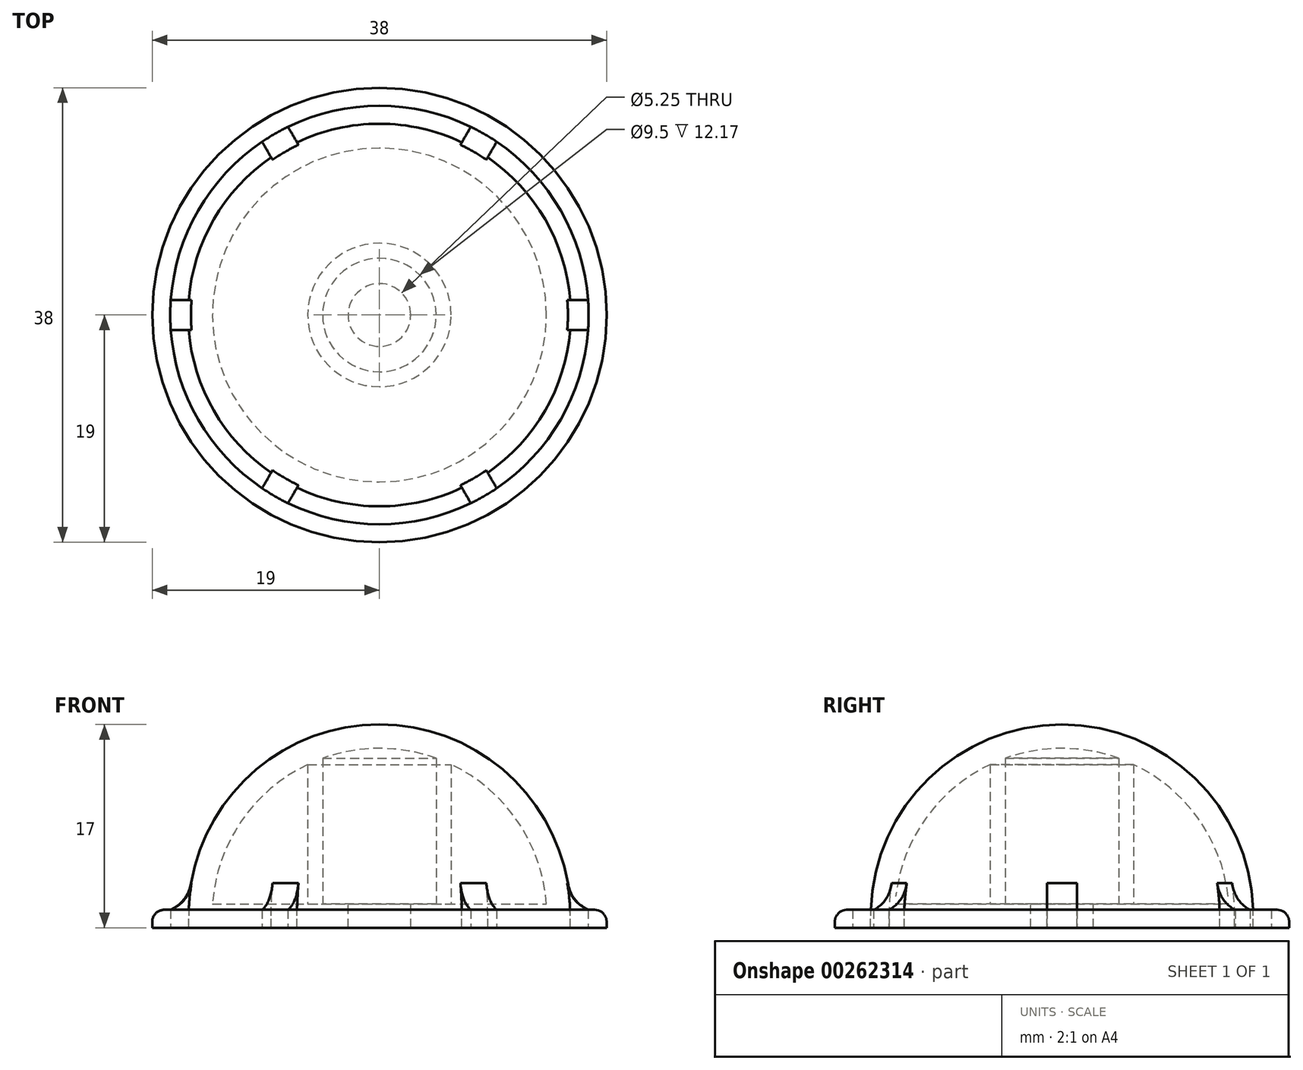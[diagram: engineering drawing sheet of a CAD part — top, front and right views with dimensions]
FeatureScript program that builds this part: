
annotation { "Feature Type Name" : "Feature", "Feature Type Description" : "" }
export const myFeature = defineFeature(function(context is Context, id is Id, definition is map)
    precondition{}
    {
        {
            var Q0;
            Q0=qCreatedBy(makeId("Top.planeOp"),FACE);
            var sketch = newSketch(context, id + "F0", { "sketchPlane" : qUnion([Q0])});
            skArc(sketch, "E0", {"start": v(0, -16) * mm, "mid": v(16, 0) * mm, "end": v(0, 16) * mm});
            skLineSegment(sketch, "E1", {"start": v(0, 16) * mm, "end": v(0, -16) * mm});
            skSolve(sketch);
        }
        {
            var Q0;
            Q0=makeQuery(id+"F0.imprint","IMPRINT",FACE,{"disambiguationData":[TD([[makeQuery(id+"F0.imprint","IMPRINT",EDGE,{"derivedFrom":sQuery(id+"F0.wireOp",EDGE,"E0")}),1.0]])]});
            var Q1;
            Q1=sQuery(id+"F0.wireOp",EDGE,"E1");
            revolve(context, id + "F1", {"entities" : qUnion([Q0]), "axis" : qUnion([Q1]), "revolveType" : RevolveType.ONE_DIRECTION, "angle" : 180 * degree});
        }
        {
            var Q0;
            Q0=makeQuery(id+"F1.opRevolve","CAP_FACE",FACE,{"disambiguationData":[OSD([sQuery(id+"F0.wireOp",EDGE,"E0"),sQuery(id+"F0.wireOp",EDGE,"E1")])],"isStart":true});
            var sketch = newSketch(context, id + "F2", { "sketchPlane" : qUnion([Q0])});
            skCircle(sketch, "E2", {"center": v(0, 0) * mm, "radius": 2.62 * mm});
            skSolve(sketch);
        }
        {
            var Q0;
            Q0=makeQuery(id+"F2.imprint","IMPRINT",FACE,{"disambiguationData":[TD([[makeQuery(id+"F2.imprint","IMPRINT",EDGE,{"derivedFrom":sQuery(id+"F2.wireOp",EDGE,"E2")}),-1.0]])]});
            extrude(context, id + "F3", {"entities" : qUnion([Q0]), "operationType" : NewBodyOperationType.ADD, "depth" : 1 * mm});
        }
        {
            var Q0;
            Q0=makeQuery(id+"F1.opRevolve","CAP_FACE",FACE,{"disambiguationData":[OSD([sQuery(id+"F0.wireOp",EDGE,"E0"),sQuery(id+"F0.wireOp",EDGE,"E1")])],"isStart":true});
            shell(context, id + "F4", {"entities" : qUnion([Q0]), "thickness" : 2 * mm});
        }
        {
            var Q0;
            Q0=makeQuery(id+"F4.opShell","OFFSET_FACE",FACE,{"disambiguationData":[OSD([sQuery(id+"F0.wireOp",EDGE,"E0"),sQuery(id+"F2.wireOp",EDGE,"E2")])]});
            var sketch = newSketch(context, id + "F5", { "sketchPlane" : qUnion([Q0])});
            skCircle(sketch, "E3", {"center": v(0, 0) * mm, "radius": 6 * mm});
            skCircle(sketch, "E4", {"center": v(0, 0) * mm, "radius": 4.75 * mm});
            skSolve(sketch);
        }
        {
            var Q0;
            Q0=makeQuery(id+"F5.imprint","IMPRINT",FACE,{"disambiguationData":[TD([[makeQuery(id+"F5.imprint","IMPRINT",EDGE,{"derivedFrom":sQuery(id+"F5.wireOp",EDGE,"E3")}),1.0]])]});
            extrude(context, id + "F6", {"entities" : qUnion([Q0]), "operationType" : NewBodyOperationType.ADD, "endBound" : BoundingType.UP_TO_NEXT, "depth" : 25 * mm});
        }
        {
            var Q0;
            Q0=makeQuery(id+"F3.opExtrude","CAP_FACE",FACE,{"disambiguationData":[OSD([sQuery(id+"F0.wireOp",EDGE,"E0"),sQuery(id+"F2.wireOp",EDGE,"E2")])],"isStart":false});
            var sketch = newSketch(context, id + "F7", { "sketchPlane" : qUnion([Q0])});
            skCircle(sketch, "E5", {"center": v(0, 0) * mm, "radius": 19 * mm});
            skCircle(sketch, "E6", {"center": v(0, 0) * mm, "radius": 17.5 * mm});
            skLineSegment(sketch, "E7.bottom", {"start": v(-17.46, -1.25) * mm, "end": v(-15.25, -1.25) * mm});
            skLineSegment(sketch, "E7.top", {"start": v(-17.46, 1.25) * mm, "end": v(-15.25, 1.25) * mm});
            skLineSegment(sketch, "E7.right", {"start": v(-15.25, -1.25) * mm, "end": v(-15.25, 1.25) * mm});
            skPoint(sketch, "E7.middle", {"position": v(-16.75, 0) * mm});
            skPoint(sketch, "E8.orphan", {"position": v(-18.25, 1.25) * mm});
            skPoint(sketch, "E9.orphan", {"position": v(-18.25, -1.25) * mm});
            skLineSegment(sketch, "E10.1.0", {"start": v(-9.81, -14.5) * mm, "end": v(-8.7, -12.58) * mm});
            skLineSegment(sketch, "E10.1.1", {"start": v(-6.54, -13.83) * mm, "end": v(-8.7, -12.58) * mm});
            skLineSegment(sketch, "E10.1.2", {"start": v(-7.65, -15.74) * mm, "end": v(-6.54, -13.83) * mm});
            skLineSegment(sketch, "E10.2.0", {"start": v(7.65, -15.74) * mm, "end": v(6.54, -13.83) * mm});
            skLineSegment(sketch, "E10.2.1", {"start": v(8.7, -12.58) * mm, "end": v(6.54, -13.83) * mm});
            skLineSegment(sketch, "E10.2.2", {"start": v(9.81, -14.5) * mm, "end": v(8.7, -12.58) * mm});
            skLineSegment(sketch, "E10.3.0", {"start": v(17.46, -1.25) * mm, "end": v(15.25, -1.25) * mm});
            skLineSegment(sketch, "E10.3.1", {"start": v(15.25, 1.25) * mm, "end": v(15.25, -1.25) * mm});
            skLineSegment(sketch, "E10.3.2", {"start": v(17.46, 1.25) * mm, "end": v(15.25, 1.25) * mm});
            skLineSegment(sketch, "E10.4.0", {"start": v(9.81, 14.5) * mm, "end": v(8.7, 12.58) * mm});
            skLineSegment(sketch, "E10.4.1", {"start": v(6.54, 13.83) * mm, "end": v(8.7, 12.58) * mm});
            skLineSegment(sketch, "E10.4.2", {"start": v(7.65, 15.74) * mm, "end": v(6.54, 13.83) * mm});
            skLineSegment(sketch, "E11.1.5.0", {"start": v(-7.65, 15.74) * mm, "end": v(-6.54, 13.83) * mm});
            skLineSegment(sketch, "E11.3.5.0", {"start": v(-8.7, 12.58) * mm, "end": v(-6.54, 13.83) * mm});
            skLineSegment(sketch, "E11.6.5.0", {"start": v(-9.81, 14.5) * mm, "end": v(-8.7, 12.58) * mm});
            skSolve(sketch);
        }
        {
            var Q0;
            Q0=makeQuery(id+"F7.imprint","IMPRINT",FACE,{"disambiguationData":[TD([[makeQuery(id+"F7.imprint","IMPRINT",EDGE,{"derivedFrom":sQuery(id+"F7.wireOp",EDGE,"E5")}),1.0]])]});
            var Q1;
            {var subQ0=sQuery(id+"F7.wireOp",EDGE,"E7.bottom");Q1=makeQuery(id+"F7.imprint","IMPRINT",FACE,{"disambiguationData":[TD([[makeQuery(id+"F7.imprint","IMPRINT",EDGE,{"derivedFrom":subQ0}),1.0]])]});}
            var Q2;
            {var subQ0=sQuery(id+"F7.wireOp",EDGE,"E10.1.0");Q2=makeQuery(id+"F7.imprint","IMPRINT",FACE,{"disambiguationData":[TD([[makeQuery(id+"F7.imprint","IMPRINT",EDGE,{"derivedFrom":subQ0}),-1.0]])]});}
            var Q3;
            {var subQ0=sQuery(id+"F7.wireOp",EDGE,"E10.2.0");Q3=makeQuery(id+"F7.imprint","IMPRINT",FACE,{"disambiguationData":[TD([[makeQuery(id+"F7.imprint","IMPRINT",EDGE,{"derivedFrom":subQ0}),-1.0]])]});}
            var Q4;
            {var subQ0=sQuery(id+"F7.wireOp",EDGE,"E10.3.0");Q4=makeQuery(id+"F7.imprint","IMPRINT",FACE,{"disambiguationData":[TD([[makeQuery(id+"F7.imprint","IMPRINT",EDGE,{"derivedFrom":subQ0}),-1.0]])]});}
            var Q5;
            {var subQ0=sQuery(id+"F7.wireOp",EDGE,"E10.4.0");Q5=makeQuery(id+"F7.imprint","IMPRINT",FACE,{"disambiguationData":[TD([[makeQuery(id+"F7.imprint","IMPRINT",EDGE,{"derivedFrom":subQ0}),-1.0]])]});}
            var Q6;
            {var subQ0=sQuery(id+"F7.wireOp",EDGE,"E11.1.5.0");Q6=makeQuery(id+"F7.imprint","IMPRINT",FACE,{"disambiguationData":[TD([[makeQuery(id+"F7.imprint","IMPRINT",EDGE,{"derivedFrom":subQ0}),-1.0]])]});}
            extrude(context, id + "F8", {"entities" : qUnion([Q0, Q1, Q2, Q3, Q4, Q5, Q6]), "operationType" : NewBodyOperationType.ADD, "oppositeDirection" : true, "depth" : 1.5 * mm});
        }
        {
            var Q0;
            Q0=makeQuery(id+"F8.boolean.opBoolean","INTERSECT",EDGE,{"disambiguationData":[OD(2.0)],"derivedFrom":[makeQuery(id+"F1.opRevolve","SWEPT_FACE",FACE,{"disambiguationData":[OSD([sQuery(id+"F0.wireOp",EDGE,"E0")])]}),makeQuery(id+"F8.opExtrude","CAP_FACE",FACE,{"disambiguationData":[OSD([sQuery(id+"F7.wireOp",EDGE,"E5"),sQuery(id+"F7.wireOp",EDGE,"E6"),sQuery(id+"F7.wireOp",EDGE,"E7.bottom"),sQuery(id+"F7.wireOp",EDGE,"E7.top"),sQuery(id+"F7.wireOp",EDGE,"E7.right"),sQuery(id+"F7.wireOp",EDGE,"E10.1.0"),sQuery(id+"F7.wireOp",EDGE,"E10.1.1"),sQuery(id+"F7.wireOp",EDGE,"E10.1.2"),sQuery(id+"F7.wireOp",EDGE,"E10.2.0"),sQuery(id+"F7.wireOp",EDGE,"E10.2.1"),sQuery(id+"F7.wireOp",EDGE,"E10.2.2"),sQuery(id+"F7.wireOp",EDGE,"E10.3.0"),sQuery(id+"F7.wireOp",EDGE,"E10.3.1"),sQuery(id+"F7.wireOp",EDGE,"E10.3.2"),sQuery(id+"F7.wireOp",EDGE,"E10.4.0"),sQuery(id+"F7.wireOp",EDGE,"E10.4.1"),sQuery(id+"F7.wireOp",EDGE,"E10.4.2"),sQuery(id+"F7.wireOp",EDGE,"E11.1.5.0"),sQuery(id+"F7.wireOp",EDGE,"E11.3.5.0"),sQuery(id+"F7.wireOp",EDGE,"E11.6.5.0")])],"isStart":false})]});
            var Q1;
            Q1=makeQuery(id+"F8.boolean.opBoolean","INTERSECT",EDGE,{"disambiguationData":[OD(3.0)],"derivedFrom":[makeQuery(id+"F1.opRevolve","SWEPT_FACE",FACE,{"disambiguationData":[OSD([sQuery(id+"F0.wireOp",EDGE,"E0")])]}),makeQuery(id+"F8.opExtrude","CAP_FACE",FACE,{"disambiguationData":[OSD([sQuery(id+"F7.wireOp",EDGE,"E5"),sQuery(id+"F7.wireOp",EDGE,"E6"),sQuery(id+"F7.wireOp",EDGE,"E7.bottom"),sQuery(id+"F7.wireOp",EDGE,"E7.top"),sQuery(id+"F7.wireOp",EDGE,"E7.right"),sQuery(id+"F7.wireOp",EDGE,"E10.1.0"),sQuery(id+"F7.wireOp",EDGE,"E10.1.1"),sQuery(id+"F7.wireOp",EDGE,"E10.1.2"),sQuery(id+"F7.wireOp",EDGE,"E10.2.0"),sQuery(id+"F7.wireOp",EDGE,"E10.2.1"),sQuery(id+"F7.wireOp",EDGE,"E10.2.2"),sQuery(id+"F7.wireOp",EDGE,"E10.3.0"),sQuery(id+"F7.wireOp",EDGE,"E10.3.1"),sQuery(id+"F7.wireOp",EDGE,"E10.3.2"),sQuery(id+"F7.wireOp",EDGE,"E10.4.0"),sQuery(id+"F7.wireOp",EDGE,"E10.4.1"),sQuery(id+"F7.wireOp",EDGE,"E10.4.2"),sQuery(id+"F7.wireOp",EDGE,"E11.1.5.0"),sQuery(id+"F7.wireOp",EDGE,"E11.3.5.0"),sQuery(id+"F7.wireOp",EDGE,"E11.6.5.0")])],"isStart":false})]});
            var Q2;
            Q2=makeQuery(id+"F8.boolean.opBoolean","INTERSECT",EDGE,{"disambiguationData":[OD(4.0)],"derivedFrom":[makeQuery(id+"F1.opRevolve","SWEPT_FACE",FACE,{"disambiguationData":[OSD([sQuery(id+"F0.wireOp",EDGE,"E0")])]}),makeQuery(id+"F8.opExtrude","CAP_FACE",FACE,{"disambiguationData":[OSD([sQuery(id+"F7.wireOp",EDGE,"E5"),sQuery(id+"F7.wireOp",EDGE,"E6"),sQuery(id+"F7.wireOp",EDGE,"E7.bottom"),sQuery(id+"F7.wireOp",EDGE,"E7.top"),sQuery(id+"F7.wireOp",EDGE,"E7.right"),sQuery(id+"F7.wireOp",EDGE,"E10.1.0"),sQuery(id+"F7.wireOp",EDGE,"E10.1.1"),sQuery(id+"F7.wireOp",EDGE,"E10.1.2"),sQuery(id+"F7.wireOp",EDGE,"E10.2.0"),sQuery(id+"F7.wireOp",EDGE,"E10.2.1"),sQuery(id+"F7.wireOp",EDGE,"E10.2.2"),sQuery(id+"F7.wireOp",EDGE,"E10.3.0"),sQuery(id+"F7.wireOp",EDGE,"E10.3.1"),sQuery(id+"F7.wireOp",EDGE,"E10.3.2"),sQuery(id+"F7.wireOp",EDGE,"E10.4.0"),sQuery(id+"F7.wireOp",EDGE,"E10.4.1"),sQuery(id+"F7.wireOp",EDGE,"E10.4.2"),sQuery(id+"F7.wireOp",EDGE,"E11.1.5.0"),sQuery(id+"F7.wireOp",EDGE,"E11.3.5.0"),sQuery(id+"F7.wireOp",EDGE,"E11.6.5.0")])],"isStart":false})]});
            var Q3;
            Q3=makeQuery(id+"F8.boolean.opBoolean","INTERSECT",EDGE,{"disambiguationData":[OD(1.0)],"derivedFrom":[makeQuery(id+"F1.opRevolve","SWEPT_FACE",FACE,{"disambiguationData":[OSD([sQuery(id+"F0.wireOp",EDGE,"E0")])]}),makeQuery(id+"F8.opExtrude","CAP_FACE",FACE,{"disambiguationData":[OSD([sQuery(id+"F7.wireOp",EDGE,"E5"),sQuery(id+"F7.wireOp",EDGE,"E6"),sQuery(id+"F7.wireOp",EDGE,"E7.bottom"),sQuery(id+"F7.wireOp",EDGE,"E7.top"),sQuery(id+"F7.wireOp",EDGE,"E7.right"),sQuery(id+"F7.wireOp",EDGE,"E10.1.0"),sQuery(id+"F7.wireOp",EDGE,"E10.1.1"),sQuery(id+"F7.wireOp",EDGE,"E10.1.2"),sQuery(id+"F7.wireOp",EDGE,"E10.2.0"),sQuery(id+"F7.wireOp",EDGE,"E10.2.1"),sQuery(id+"F7.wireOp",EDGE,"E10.2.2"),sQuery(id+"F7.wireOp",EDGE,"E10.3.0"),sQuery(id+"F7.wireOp",EDGE,"E10.3.1"),sQuery(id+"F7.wireOp",EDGE,"E10.3.2"),sQuery(id+"F7.wireOp",EDGE,"E10.4.0"),sQuery(id+"F7.wireOp",EDGE,"E10.4.1"),sQuery(id+"F7.wireOp",EDGE,"E10.4.2"),sQuery(id+"F7.wireOp",EDGE,"E11.1.5.0"),sQuery(id+"F7.wireOp",EDGE,"E11.3.5.0"),sQuery(id+"F7.wireOp",EDGE,"E11.6.5.0")])],"isStart":false})]});
            var Q4;
            Q4=makeQuery(id+"F8.boolean.opBoolean","INTERSECT",EDGE,{"disambiguationData":[OD(0.0)],"derivedFrom":[makeQuery(id+"F1.opRevolve","SWEPT_FACE",FACE,{"disambiguationData":[OSD([sQuery(id+"F0.wireOp",EDGE,"E0")])]}),makeQuery(id+"F8.opExtrude","CAP_FACE",FACE,{"disambiguationData":[OSD([sQuery(id+"F7.wireOp",EDGE,"E5"),sQuery(id+"F7.wireOp",EDGE,"E6"),sQuery(id+"F7.wireOp",EDGE,"E7.bottom"),sQuery(id+"F7.wireOp",EDGE,"E7.top"),sQuery(id+"F7.wireOp",EDGE,"E7.right"),sQuery(id+"F7.wireOp",EDGE,"E10.1.0"),sQuery(id+"F7.wireOp",EDGE,"E10.1.1"),sQuery(id+"F7.wireOp",EDGE,"E10.1.2"),sQuery(id+"F7.wireOp",EDGE,"E10.2.0"),sQuery(id+"F7.wireOp",EDGE,"E10.2.1"),sQuery(id+"F7.wireOp",EDGE,"E10.2.2"),sQuery(id+"F7.wireOp",EDGE,"E10.3.0"),sQuery(id+"F7.wireOp",EDGE,"E10.3.1"),sQuery(id+"F7.wireOp",EDGE,"E10.3.2"),sQuery(id+"F7.wireOp",EDGE,"E10.4.0"),sQuery(id+"F7.wireOp",EDGE,"E10.4.1"),sQuery(id+"F7.wireOp",EDGE,"E10.4.2"),sQuery(id+"F7.wireOp",EDGE,"E11.1.5.0"),sQuery(id+"F7.wireOp",EDGE,"E11.3.5.0"),sQuery(id+"F7.wireOp",EDGE,"E11.6.5.0")])],"isStart":false})]});
            var Q5;
            Q5=makeQuery(id+"F8.boolean.opBoolean","INTERSECT",EDGE,{"disambiguationData":[OD(5.0)],"derivedFrom":[makeQuery(id+"F1.opRevolve","SWEPT_FACE",FACE,{"disambiguationData":[OSD([sQuery(id+"F0.wireOp",EDGE,"E0")])]}),makeQuery(id+"F8.opExtrude","CAP_FACE",FACE,{"disambiguationData":[OSD([sQuery(id+"F7.wireOp",EDGE,"E5"),sQuery(id+"F7.wireOp",EDGE,"E6"),sQuery(id+"F7.wireOp",EDGE,"E7.bottom"),sQuery(id+"F7.wireOp",EDGE,"E7.top"),sQuery(id+"F7.wireOp",EDGE,"E7.right"),sQuery(id+"F7.wireOp",EDGE,"E10.1.0"),sQuery(id+"F7.wireOp",EDGE,"E10.1.1"),sQuery(id+"F7.wireOp",EDGE,"E10.1.2"),sQuery(id+"F7.wireOp",EDGE,"E10.2.0"),sQuery(id+"F7.wireOp",EDGE,"E10.2.1"),sQuery(id+"F7.wireOp",EDGE,"E10.2.2"),sQuery(id+"F7.wireOp",EDGE,"E10.3.0"),sQuery(id+"F7.wireOp",EDGE,"E10.3.1"),sQuery(id+"F7.wireOp",EDGE,"E10.3.2"),sQuery(id+"F7.wireOp",EDGE,"E10.4.0"),sQuery(id+"F7.wireOp",EDGE,"E10.4.1"),sQuery(id+"F7.wireOp",EDGE,"E10.4.2"),sQuery(id+"F7.wireOp",EDGE,"E11.1.5.0"),sQuery(id+"F7.wireOp",EDGE,"E11.3.5.0"),sQuery(id+"F7.wireOp",EDGE,"E11.6.5.0")])],"isStart":false})]});
            fillet(context, id + "F9", {"entities" : qUnion([Q0, Q1, Q2, Q3, Q4, Q5]), "radius" : 3 * mm, "tangentPropagation" : true, "rho" : 0.5, "crossSection" : FilletCrossSection.CONIC, "allowEdgeOverflow" : false});
        }
        {
            var Q0;
            Q0=makeQuery(id+"F8.opExtrude","CAP_EDGE",EDGE,{"disambiguationData":[OSD([sQuery(id+"F7.wireOp",EDGE,"E5")])],"isStart":false});
            fillet(context, id + "F10", {"entities" : qUnion([Q0]), "radius" : 1 * mm, "tangentPropagation" : true, "allowEdgeOverflow" : false});
        }
        {
            var Q0;
            Q0=makeQuery(id+"F1.opRevolve","CAP_FACE",FACE,{"disambiguationData":[OSD([sQuery(id+"F0.wireOp",EDGE,"E0"),sQuery(id+"F0.wireOp",EDGE,"E1")])],"isStart":true});
            extrude(context, id + "F11", {"entities" : qUnion([Q0]), "operationType" : NewBodyOperationType.REMOVE, "oppositeDirection" : true, "depth" : 5 * mm});
        }
    });
